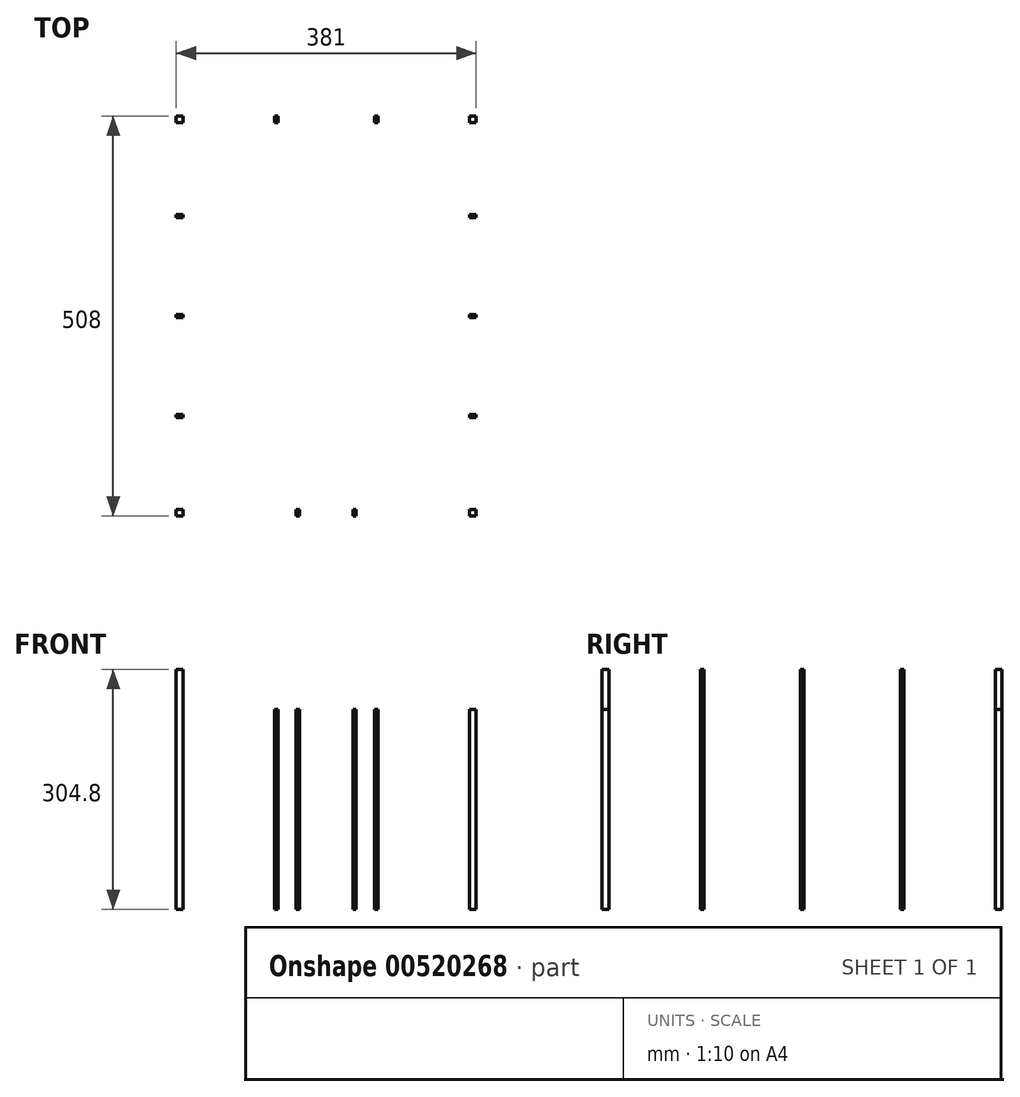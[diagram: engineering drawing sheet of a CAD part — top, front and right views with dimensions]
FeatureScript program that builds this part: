
annotation { "Feature Type Name" : "Feature", "Feature Type Description" : "" }
export const myFeature = defineFeature(function(context is Context, id is Id, definition is map)
    precondition{}
    {
        {
            var Q0;
            Q0=qCreatedBy(makeId("Top.planeOp"),FACE);
            var sketch = newSketch(context, id + "F0", { "sketchPlane" : qUnion([Q0])});
            skLineSegment(sketch, "E0", {"start": v(-190.5, 0) * mm, "end": v(190.5, 0) * mm, "construction": true});
            skLineSegment(sketch, "E1", {"start": v(0, 254) * mm, "end": v(0, -254) * mm, "construction": true});
            skLineSegment(sketch, "E2", {"start": v(-190.5, 254) * mm, "end": v(-182.03, 254) * mm});
            skLineSegment(sketch, "E3", {"start": v(-182.03, 254) * mm, "end": v(-182.03, 245.53) * mm});
            skLineSegment(sketch, "E4", {"start": v(-182.03, 245.53) * mm, "end": v(-190.5, 245.53) * mm});
            skLineSegment(sketch, "E5", {"start": v(-190.5, 245.53) * mm, "end": v(-190.5, 254) * mm});
            skLineSegment(sketch, "E6.MirrorCS", {"start": v(190.5, 254) * mm, "end": v(182.03, 254) * mm});
            skLineSegment(sketch, "E7.MirrorCS", {"start": v(182.03, 245.53) * mm, "end": v(190.5, 245.53) * mm});
            skLineSegment(sketch, "E8.MirrorCS", {"start": v(182.03, 254) * mm, "end": v(182.03, 245.53) * mm});
            skLineSegment(sketch, "E9.MirrorCS", {"start": v(190.5, 245.53) * mm, "end": v(190.5, 254) * mm});
            skLineSegment(sketch, "E10.MirrorCS", {"start": v(190.5, 0) * mm, "end": v(-190.5, 0) * mm, "construction": true});
            skLineSegment(sketch, "E11.MirrorCS", {"start": v(-190.5, -254) * mm, "end": v(-182.03, -254) * mm});
            skLineSegment(sketch, "E12.MirrorCS", {"start": v(-190.5, -245.53) * mm, "end": v(-190.5, -254) * mm});
            skLineSegment(sketch, "E13.MirrorCS", {"start": v(-182.03, -245.53) * mm, "end": v(-190.5, -245.53) * mm});
            skLineSegment(sketch, "E14.MirrorCS", {"start": v(-182.03, -254) * mm, "end": v(-182.03, -245.53) * mm});
            skLineSegment(sketch, "E15.MirrorCS", {"start": v(190.5, -245.53) * mm, "end": v(190.5, -254) * mm});
            skLineSegment(sketch, "E16.MirrorCS", {"start": v(182.03, -245.53) * mm, "end": v(190.5, -245.53) * mm});
            skLineSegment(sketch, "E17.MirrorCS", {"start": v(190.5, -254) * mm, "end": v(182.03, -254) * mm});
            skLineSegment(sketch, "E18.MirrorCS", {"start": v(182.03, -254) * mm, "end": v(182.03, -245.53) * mm});
            skLineSegment(sketch, "E19", {"start": v(-190.5, 0) * mm, "end": v(-190.5, 2.12) * mm});
            skLineSegment(sketch, "E20", {"start": v(-190.5, 2.12) * mm, "end": v(-182.03, 2.12) * mm});
            skLineSegment(sketch, "E21", {"start": v(-182.03, 2.12) * mm, "end": v(-182.03, -2.12) * mm});
            skLineSegment(sketch, "E22", {"start": v(-182.03, -2.12) * mm, "end": v(-190.5, -2.12) * mm});
            skLineSegment(sketch, "E23", {"start": v(-190.5, -2.12) * mm, "end": v(-190.5, 0) * mm});
            skLineSegment(sketch, "E24", {"start": v(-190.5, 0) * mm, "end": v(-190.5, -254) * mm, "construction": true});
            skLineSegment(sketch, "E25", {"start": v(-190.5, 254) * mm, "end": v(-190.5, 0) * mm, "construction": true});
            skPoint(sketch, "E26", {"position": v(-190.5, 127) * mm});
            skPoint(sketch, "E27", {"position": v(-190.5, -127) * mm});
            skLineSegment(sketch, "E28", {"start": v(-190.5, 127) * mm, "end": v(-190.5, 129.12) * mm});
            skLineSegment(sketch, "E29", {"start": v(-190.5, 129.12) * mm, "end": v(-182.03, 129.12) * mm});
            skLineSegment(sketch, "E30", {"start": v(-182.03, 129.12) * mm, "end": v(-182.03, 124.88) * mm});
            skLineSegment(sketch, "E31", {"start": v(-182.03, 124.88) * mm, "end": v(-190.5, 124.88) * mm});
            skLineSegment(sketch, "E32", {"start": v(-190.5, 124.88) * mm, "end": v(-190.5, 127) * mm});
            skLineSegment(sketch, "E33", {"start": v(-190.5, -127) * mm, "end": v(-190.5, -129.12) * mm});
            skLineSegment(sketch, "E34", {"start": v(-190.5, -129.12) * mm, "end": v(-182.03, -129.12) * mm});
            skLineSegment(sketch, "E35", {"start": v(-182.03, -129.12) * mm, "end": v(-182.03, -124.88) * mm});
            skLineSegment(sketch, "E36", {"start": v(-182.03, -124.88) * mm, "end": v(-190.5, -124.88) * mm});
            skLineSegment(sketch, "E37", {"start": v(-190.5, -124.88) * mm, "end": v(-190.5, -127) * mm});
            skLineSegment(sketch, "E38.MirrorCS", {"start": v(190.5, 127) * mm, "end": v(190.5, 129.12) * mm});
            skLineSegment(sketch, "E39.MirrorCS", {"start": v(190.5, 124.88) * mm, "end": v(190.5, 127) * mm});
            skLineSegment(sketch, "E40.MirrorCS", {"start": v(190.5, 129.12) * mm, "end": v(182.03, 129.12) * mm});
            skPoint(sketch, "E41.MirrorP", {"position": v(190.5, 127) * mm});
            skLineSegment(sketch, "E42.MirrorCS", {"start": v(182.03, 124.88) * mm, "end": v(190.5, 124.88) * mm});
            skLineSegment(sketch, "E43.MirrorCS", {"start": v(182.03, 129.12) * mm, "end": v(182.03, 124.88) * mm});
            skLineSegment(sketch, "E44.MirrorCS", {"start": v(190.5, 254) * mm, "end": v(190.5, 0) * mm, "construction": true});
            skLineSegment(sketch, "E45.MirrorCS", {"start": v(190.5, -2.12) * mm, "end": v(190.5, 0) * mm});
            skLineSegment(sketch, "E46.MirrorCS", {"start": v(190.5, 0) * mm, "end": v(190.5, 2.12) * mm});
            skLineSegment(sketch, "E47.MirrorCS", {"start": v(190.5, 2.12) * mm, "end": v(182.03, 2.12) * mm});
            skLineSegment(sketch, "E48.MirrorCS", {"start": v(182.03, -2.12) * mm, "end": v(190.5, -2.12) * mm});
            skLineSegment(sketch, "E49.MirrorCS", {"start": v(182.03, 2.12) * mm, "end": v(182.03, -2.12) * mm});
            skLineSegment(sketch, "E50.MirrorCS", {"start": v(190.5, 0) * mm, "end": v(190.5, -254) * mm, "construction": true});
            skLineSegment(sketch, "E51.MirrorCS", {"start": v(190.5, -124.88) * mm, "end": v(190.5, -127) * mm});
            skLineSegment(sketch, "E52.MirrorCS", {"start": v(190.5, -127) * mm, "end": v(190.5, -129.12) * mm});
            skLineSegment(sketch, "E53.MirrorCS", {"start": v(182.03, -124.88) * mm, "end": v(190.5, -124.88) * mm});
            skLineSegment(sketch, "E54.MirrorCS", {"start": v(190.5, -129.12) * mm, "end": v(182.03, -129.12) * mm});
            skPoint(sketch, "E55.MirrorP", {"position": v(190.5, -127) * mm});
            skLineSegment(sketch, "E56.MirrorCS", {"start": v(182.03, -129.12) * mm, "end": v(182.03, -124.88) * mm});
            skLineSegment(sketch, "E57", {"start": v(-190.5, -254) * mm, "end": v(190.5, -254) * mm, "construction": true});
            skLineSegment(sketch, "E58", {"start": v(-33.87, -254) * mm, "end": v(33.87, -254) * mm});
            skLineSegment(sketch, "E59", {"start": v(-33.87, -254) * mm, "end": v(-33.87, -245.53) * mm});
            skLineSegment(sketch, "E60", {"start": v(-33.87, -245.53) * mm, "end": v(-38.1, -245.53) * mm});
            skLineSegment(sketch, "E61", {"start": v(-38.1, -245.53) * mm, "end": v(-38.1, -254) * mm});
            skLineSegment(sketch, "E62", {"start": v(-38.1, -254) * mm, "end": v(-33.87, -254) * mm});
            skLineSegment(sketch, "E63", {"start": v(33.87, -254) * mm, "end": v(33.87, -245.53) * mm});
            skLineSegment(sketch, "E64", {"start": v(33.87, -245.53) * mm, "end": v(38.1, -245.53) * mm});
            skLineSegment(sketch, "E65", {"start": v(38.1, -245.53) * mm, "end": v(38.1, -254) * mm});
            skLineSegment(sketch, "E66", {"start": v(38.1, -254) * mm, "end": v(33.87, -254) * mm});
            skLineSegment(sketch, "E67", {"start": v(-190.5, 254) * mm, "end": v(190.5, 254) * mm, "construction": true});
            skLineSegment(sketch, "E68", {"start": v(-65.62, 254) * mm, "end": v(-65.62, 245.53) * mm});
            skLineSegment(sketch, "E69", {"start": v(-65.62, 245.53) * mm, "end": v(-61.38, 245.53) * mm});
            skLineSegment(sketch, "E70", {"start": v(-61.38, 245.53) * mm, "end": v(-61.38, 254) * mm});
            skLineSegment(sketch, "E71", {"start": v(-61.38, 254) * mm, "end": v(-65.62, 254) * mm});
            skLineSegment(sketch, "E72", {"start": v(61.38, 254) * mm, "end": v(61.38, 245.53) * mm});
            skLineSegment(sketch, "E73", {"start": v(61.38, 245.53) * mm, "end": v(65.62, 245.53) * mm});
            skLineSegment(sketch, "E74", {"start": v(65.62, 245.53) * mm, "end": v(65.62, 254) * mm});
            skLineSegment(sketch, "E75", {"start": v(65.62, 254) * mm, "end": v(61.38, 254) * mm});
            skLineSegment(sketch, "E76", {"start": v(-63.5, 254) * mm, "end": v(-63.5, 245.53) * mm, "construction": true});
            skLineSegment(sketch, "E77", {"start": v(63.5, 254) * mm, "end": v(63.5, 245.53) * mm, "construction": true});
            skSolve(sketch);
        }
        {
            var Q0;
            Q0=makeQuery(id+"F0.imprint","IMPRINT",FACE,{"disambiguationData":[TD([[makeQuery(id+"F0.imprint","IMPRINT",EDGE,{"derivedFrom":sQuery(id+"F0.wireOp",EDGE,"E3")}),-1.0]])]});
            var Q1;
            Q1=makeQuery(id+"F0.imprint","IMPRINT",FACE,{"disambiguationData":[TD([[makeQuery(id+"F0.imprint","IMPRINT",EDGE,{"derivedFrom":sQuery(id+"F0.wireOp",EDGE,"E28")}),-1.0]])]});
            var Q2;
            Q2=makeQuery(id+"F0.imprint","IMPRINT",FACE,{"disambiguationData":[TD([[makeQuery(id+"F0.imprint","IMPRINT",EDGE,{"derivedFrom":sQuery(id+"F0.wireOp",EDGE,"E19")}),-1.0]])]});
            var Q3;
            Q3=makeQuery(id+"F0.imprint","IMPRINT",FACE,{"disambiguationData":[TD([[makeQuery(id+"F0.imprint","IMPRINT",EDGE,{"derivedFrom":sQuery(id+"F0.wireOp",EDGE,"E33")}),1.0]])]});
            var Q4;
            Q4=makeQuery(id+"F0.imprint","IMPRINT",FACE,{"disambiguationData":[TD([[makeQuery(id+"F0.imprint","IMPRINT",EDGE,{"derivedFrom":sQuery(id+"F0.wireOp",EDGE,"E11.MirrorCS")}),1.0]])]});
            extrude(context, id + "F1", {"entities" : qUnion([Q0, Q1, Q2, Q3, Q4]), "depth" : 304.8 * mm, "offsetDistance" : 25.4 * mm});
        }
        {
            var Q0;
            Q0=makeQuery(id+"F0.imprint","IMPRINT",FACE,{"disambiguationData":[TD([[makeQuery(id+"F0.imprint","IMPRINT",EDGE,{"derivedFrom":sQuery(id+"F0.wireOp",EDGE,"E59")}),1.0]])]});
            var Q1;
            Q1=makeQuery(id+"F0.imprint","IMPRINT",FACE,{"disambiguationData":[TD([[makeQuery(id+"F0.imprint","IMPRINT",EDGE,{"derivedFrom":sQuery(id+"F0.wireOp",EDGE,"E63")}),-1.0]])]});
            var Q2;
            Q2=makeQuery(id+"F0.imprint","IMPRINT",FACE,{"disambiguationData":[TD([[makeQuery(id+"F0.imprint","IMPRINT",EDGE,{"derivedFrom":sQuery(id+"F0.wireOp",EDGE,"E15.MirrorCS")}),-1.0]])]});
            var Q3;
            Q3=makeQuery(id+"F0.imprint","IMPRINT",FACE,{"disambiguationData":[TD([[makeQuery(id+"F0.imprint","IMPRINT",EDGE,{"derivedFrom":sQuery(id+"F0.wireOp",EDGE,"E51.MirrorCS")}),-1.0]])]});
            var Q4;
            Q4=makeQuery(id+"F0.imprint","IMPRINT",FACE,{"disambiguationData":[TD([[makeQuery(id+"F0.imprint","IMPRINT",EDGE,{"derivedFrom":sQuery(id+"F0.wireOp",EDGE,"E45.MirrorCS")}),1.0]])]});
            var Q5;
            Q5=makeQuery(id+"F0.imprint","IMPRINT",FACE,{"disambiguationData":[TD([[makeQuery(id+"F0.imprint","IMPRINT",EDGE,{"derivedFrom":sQuery(id+"F0.wireOp",EDGE,"E68")}),1.0]])]});
            var Q6;
            Q6=makeQuery(id+"F0.imprint","IMPRINT",FACE,{"disambiguationData":[TD([[makeQuery(id+"F0.imprint","IMPRINT",EDGE,{"derivedFrom":sQuery(id+"F0.wireOp",EDGE,"E72")}),1.0]])]});
            var Q7;
            Q7=makeQuery(id+"F0.imprint","IMPRINT",FACE,{"disambiguationData":[TD([[makeQuery(id+"F0.imprint","IMPRINT",EDGE,{"derivedFrom":sQuery(id+"F0.wireOp",EDGE,"E6.MirrorCS")}),1.0]])]});
            var Q8;
            Q8=makeQuery(id+"F0.imprint","IMPRINT",FACE,{"disambiguationData":[TD([[makeQuery(id+"F0.imprint","IMPRINT",EDGE,{"derivedFrom":sQuery(id+"F0.wireOp",EDGE,"E38.MirrorCS")}),1.0]])]});
            extrude(context, id + "F2", {"entities" : qUnion([Q0, Q1, Q2, Q3, Q4, Q5, Q6, Q7, Q8]), "depth" : 254 * mm, "offsetDistance" : 25.4 * mm});
        }
    });
